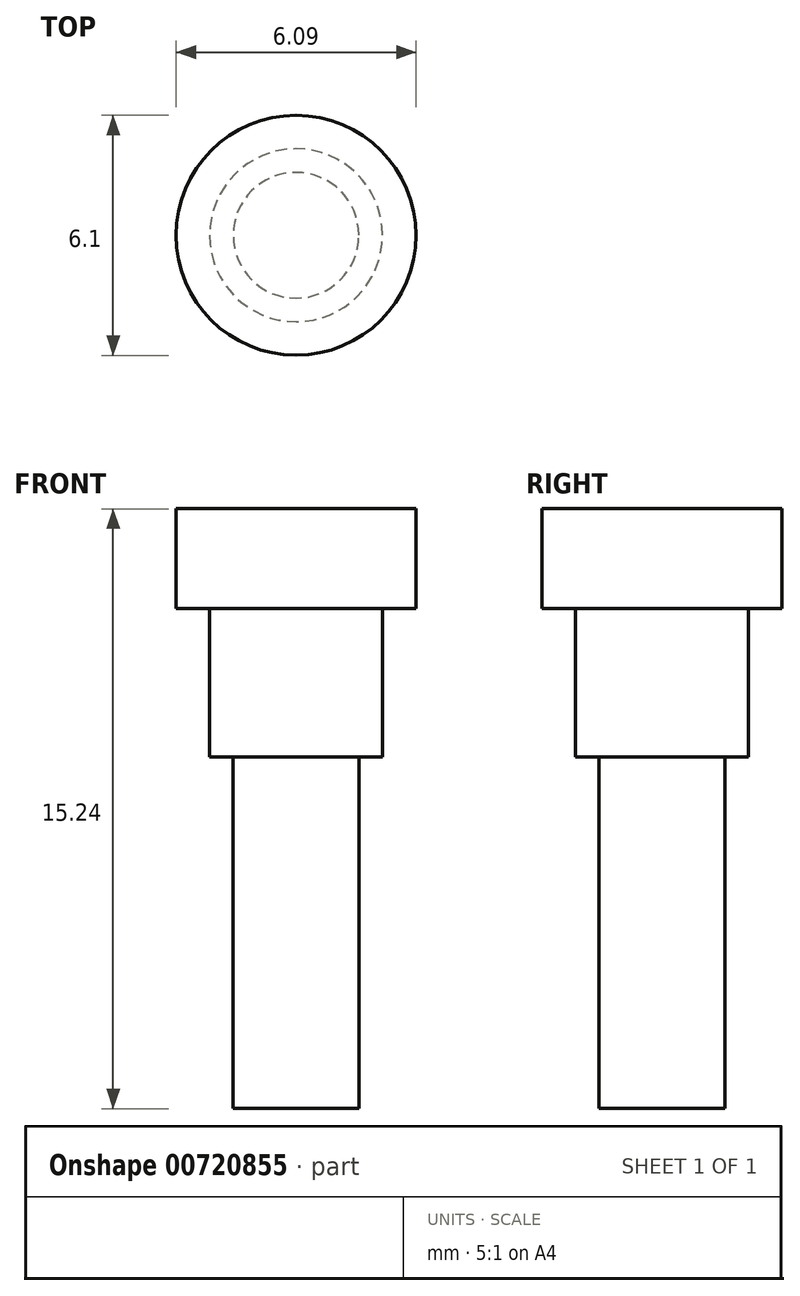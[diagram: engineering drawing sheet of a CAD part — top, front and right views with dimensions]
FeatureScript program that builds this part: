
annotation { "Feature Type Name" : "Feature", "Feature Type Description" : "" }
export const myFeature = defineFeature(function(context is Context, id is Id, definition is map)
    precondition{}
    {
        {
            var Q0;
            Q0=qCreatedBy(makeId("Front.planeOp"),FACE);
            var sketch = newSketch(context, id + "F0", { "sketchPlane" : qUnion([Q0])});
            skLineSegment(sketch, "E0", {"start": v(-59.25, -125.36) * mm, "end": v(-59.25, -127.9) * mm});
            skLineSegment(sketch, "E1", {"start": v(-59.25, -127.9) * mm, "end": v(-58.4, -127.9) * mm});
            skLineSegment(sketch, "E2", {"start": v(-58.4, -127.9) * mm, "end": v(-58.4, -131.67) * mm});
            skLineSegment(sketch, "E3", {"start": v(-58.4, -131.67) * mm, "end": v(-57.8, -131.67) * mm});
            skLineSegment(sketch, "E4", {"start": v(-57.8, -131.67) * mm, "end": v(-57.8, -140.6) * mm});
            skLineSegment(sketch, "E5", {"start": v(-57.8, -140.6) * mm, "end": v(-57.03, -140.6) * mm});
            skLineSegment(sketch, "E6", {"start": v(-56.2, -122.28) * mm, "end": v(-56.2, -145.37) * mm});
            skLineSegment(sketch, "E7", {"start": v(-59.25, -125.36) * mm, "end": v(-56.2, -125.36) * mm});
            skLineSegment(sketch, "E8", {"start": v(-57.03, -140.6) * mm, "end": v(-56.2, -140.6) * mm});
            skSolve(sketch);
        }
        {
            var Q0;
            Q0 = qSketchRegion(id + "F0", true);
            var Q1;
            Q1=sQuery(id+"F0.wireOp",EDGE,"E6");
            revolve(context, id + "F1", {"surfaceOperationType" : NewSurfaceOperationType.NEW, "entities" : qUnion([Q0]), "axis" : qUnion([Q1]), "revolveType" : RevolveType.FULL});
        }
    });
